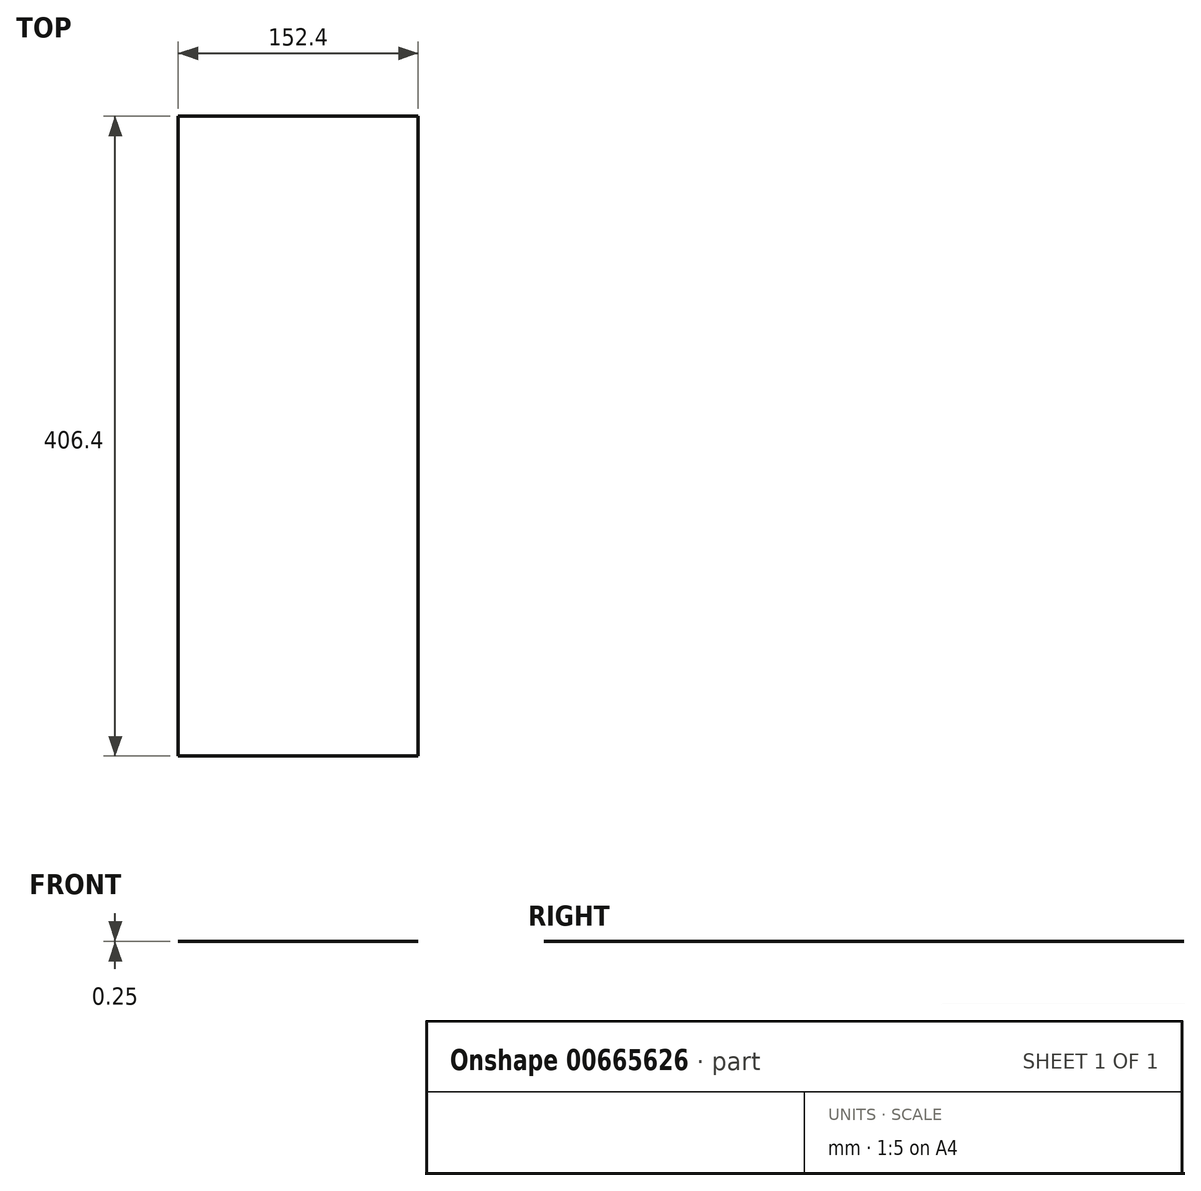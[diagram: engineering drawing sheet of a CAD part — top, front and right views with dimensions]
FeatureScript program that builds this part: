
annotation { "Feature Type Name" : "Feature", "Feature Type Description" : "" }
export const myFeature = defineFeature(function(context is Context, id is Id, definition is map)
    precondition{}
    {
        {
            var Q0;
            Q0=qCreatedBy(makeId("Top.planeOp"),FACE);
            var sketch = newSketch(context, id + "F0", { "sketchPlane" : qUnion([Q0])});
            skLineSegment(sketch, "E0.bottom", {"start": v(76.2, 203.2) * mm, "end": v(-76.2, 203.2) * mm});
            skLineSegment(sketch, "E0.top", {"start": v(76.2, -203.2) * mm, "end": v(-76.2, -203.2) * mm});
            skLineSegment(sketch, "E0.left", {"start": v(76.2, 203.2) * mm, "end": v(76.2, -203.2) * mm});
            skLineSegment(sketch, "E0.right", {"start": v(-76.2, 203.2) * mm, "end": v(-76.2, -203.2) * mm});
            skPoint(sketch, "E0.middle", {"position": v(0, 0) * mm});
            skSolve(sketch);
        }
        {
            var Q0;
            Q0 = qSketchRegion(id + "F0", true);
            extrude(context, id + "F1", {"entities" : qUnion([Q0]), "depth" : 0.25 * mm, "offsetDistance" : 25.4 * mm});
        }
    });
